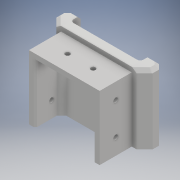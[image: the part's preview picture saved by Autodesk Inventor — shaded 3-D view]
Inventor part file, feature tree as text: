
AUTODESK INVENTOR PART (.ipt)
format: ipt  version: 2017 (Build 210142000, 142)  size: 249,856 bytes
history: native  units: mm
features: sketch x9, extrude x6, chamfer x6, hole x3, projected_geometry x2, fillet x1
ambient origin geometry x8: Origin, YZ Plane, XZ Plane, XY Plane, X Axis, Y Axis, Z Axis, Center Point
bodies: Solid1 (feature_tree)
feature tree (27):
  extrude  "Extrusion1"  Depth=40.0mm
  extrude  "Extrusion2"  Depth=20.0mm
  extrude  "Extrusion3"  Depth=12.0mm TaperAngle=0.0deg
  fillet  "Fillet1"  Radius=21.75mm
  extrude  "Extrusion4"  Depth=6.5mm TaperAngle=0.0deg
  chamfer  "Chamfer1"  Distance=3.0mm
  extrude  "Extrusion5"  Depth=4.0mm
  chamfer  "Chamfer2"  Distance=36.0mm
  hole  "Hole1"  [1 undecoded]
  hole  "Hole2"  [1 undecoded]
  chamfer  "Chamfer3"  Distance=16.0mm
  chamfer  "Chamfer4"  Distance=14.0mm
  chamfer  "Chamfer5"  Distance=2.0mm Angle=45.0deg
  chamfer  "Chamfer6"  Distance=2.0mm Angle=45.0deg
  hole  "Hole3"  [1 undecoded]
  extrude  "Extrusion6"  Depth=20.0mm
  sketch  "Sketch1"  dims[d0=44.0mm d1=40.0mm]
  sketch  "Sketch2"  dims[d2=20.0mm d3=0.0mm d4=30.0mm]
  projected_geometry  "Projected Loop1"
  sketch  "Sketch3"  dims[d5=30.0mm d6=12.0mm d7=0.0mm d8=21.75mm]
  sketch  "Sketch4"  dims[d9=21.75mm d10=6.5mm d11=0.0mm]
  projected_geometry  "Projected Loop2"
  sketch  "Sketch5"  dims[d12=2.0mm d13=3.0mm d14=0.0mm]
  sketch  "Sketch6"  dims[d15=3.0mm d16=2.0mm d17=45.0deg d18=4.0mm]
  sketch  "Sketch7"  dims[d19=4.0mm d20=36.0mm d21=0.0mm]
  sketch  "Sketch8"  dims[d22=3.0mm d23=2.0mm d24=45.0deg d25=10.0mm]
  sketch  "Sketch9"  dims[d26=10.0mm d27=2.9mm d28=6.0mm d29=4.0mm d30=2.0mm d31=90.0deg d32=8.0mm d33=20.594885mm d34=10.0mm d35=16.0mm d36=14.0mm d37=2.9mm d38=6.0mm d39=4.0mm d40=2.0mm d41=90.0deg d42=8.0mm d43=20.594885mm d44=1.0mm d45=2.0mm d46=45.0deg d47=2.0mm d48=2.0mm d49=45.0deg d50=5.0mm d51=2.0mm d52=45.0deg d53=20.0mm d54=2.0mm d55=2.0mm d56=45.0deg d57=27.0mm d58=6.2mm d59=6.0mm d60=4.0mm d61=2.0mm d62=90.0deg d63=8.0mm d64=20.594885mm d65=2.8mm d66=1.2mm d67=0.0mm]
note: 3 required parameter values undecoded (feature->parameter linkage not recoverable at this tier; creation-order binding heuristic only, values carry confidence <= 0.55)
